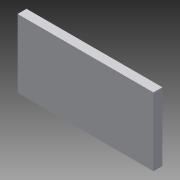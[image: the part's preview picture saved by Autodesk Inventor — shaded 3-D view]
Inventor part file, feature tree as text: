
AUTODESK INVENTOR PART (.ipt)
format: ipt  version: 2015 (Build 190159000, 159)  size: 315,392 bytes
history: native  units: mm
features: extrude x3, sketch x2
ambient origin geometry x8: Origin, YZ Plane, XZ Plane, XY Plane, X Axis, Y Axis, Z Axis, Center Point
bodies: Solid1 (feature_tree)
feature tree (5):
  sketch  "Sketch1"  dims[d2=20.0mm d51=460.0mm d52=460.0mm]
  extrude  "Extrusion1"  Depth=460.0mm
  extrude  "Extrusion2"  Depth=320.0mm TaperAngle=0.0deg
  sketch  "Sketch5"  dims[d97=20.0mm d98=0.0mm d99=320.0mm d100=0.0mm d190=20.0mm d191=300.0mm d192=0.0mm d193=20.0mm d194=460.0mm d274=4860.0mm d275=2440.0mm d276=2400.0mm d277=2400.0mm d278=720.0mm d279=450.0mm d280=20.0mm d281=470.0mm d282=740.0mm d283=20.0mm d284=700.0mm d285=510.0mm d286=260.0mm d287=20.0mm d288=280.0mm d289=550.0mm d290=740.0mm d291=550.0mm d292=20.0mm d293=530.0mm d294=890.0mm d295=280.0mm d296=20.0mm d297=260.0mm d298=870.0mm d300=870.0mm d301=20.0mm d302=550.0mm d303=260.0mm d304=20.0mm d305=540.0mm d306=570.0mm d307=20.0mm d308=590.0mm d309=1500.0mm d310=1460.0mm d311=2400.0mm d312=20.0mm d313=20.0mm d314=20.0mm d315=20.0mm d316=20.0mm d318=1660.0mm d319=20.0mm d320=720.0mm d324=20.0mm d330=720.0mm d331=740.0mm d332=470.0mm d333=20.0mm d334=20.0mm d336=530.0mm d337=510.0mm d338=260.0mm d339=20.0mm d341=550.0mm d343=550.0mm d346=870.0mm d352=460.0mm d353=460.0mm d356=460.0mm d358=460.0mm d359=460.0mm d364=460.0mm d365=460.0mm d366=460.0mm d367=460.0mm d368=460.0mm d369=480.0mm d370=460.0mm d371=460.0mm d372=460.0mm d374=910.0mm]
  extrude  "Extrusion5"  Depth=20.0mm
